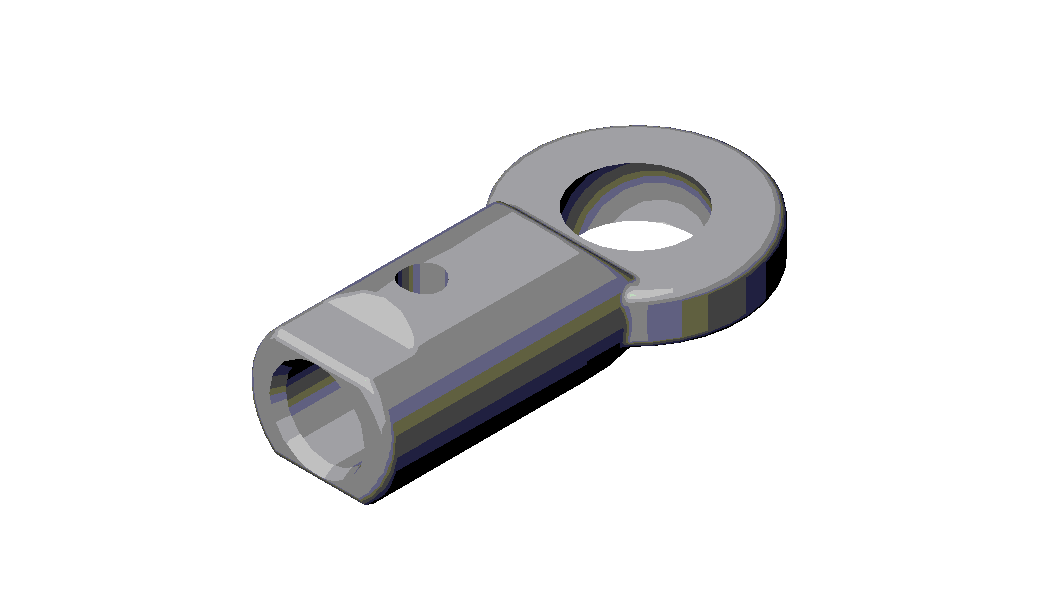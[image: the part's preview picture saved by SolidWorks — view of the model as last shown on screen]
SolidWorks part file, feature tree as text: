
SOLIDWORKS PART (.sldprt)
format: sldprt  version: not decoded by parser v0  size: 293,376 bytes
history: native  units: mm
features: sketch x7, plane x4, cut_extrude x2, fillet x2, material x1, revolve x1, extrude x1, hole x1 (+8 scaffold rows collapsed)
feature tree (27):
  scaffold x8  (default folders/planes/origin — collapsed)
  material  "Matériau <non spécifié>"
  plane  "Face"
  plane  "Dessus"
  plane  "Droite"
  plane  "Plan1"  Offset=67mm
  sketch  "Esquisse2"  dims[D1=30.0mm]
  sketch  "Esquisse1"  dims[D1=25.0mm D4=2.0mm D2=5.25mm D3=22.5mm]
  revolve  "Révolution1"  Angle=360deg
  extrude  "Extrusion2"  Depth=54mm
  sketch  "Esquisse3"  dims[c1.D1=~23.416655mm c2.D1=45.0deg c2.D2=11.0mm c2.D3=~8.19289mm c3.D3=45.0deg c3.D4=11.75mm]
  cut_extrude  "Enlèv. mat.-Extru.1"  [1 undecoded]
  fillet  "Congé5"  Radius=2mm
  fillet  "Congé7"  Radius=2mm
  sketch  "Esquisse5"
  hole  "Dégagement M1.61"  Diameter=18mm Depth=37mm
  sketch  "Esquisse11"
  sketch  "Esquisse10"  dims[hole-wizard template sketch: 39 standard entries collapsed; hole parameters kept: c13.Diamètre du perçage=18.0mm c13.Profondeur du perçage=37.0mm c13.Diamètre du fraisage entrant=20.0mm c13.D4=~33.297463mm c13.Angle du fraisage entrant=45.0deg c14.D5=~14.816244mm c14.Angle de pointe=118.0deg]
  sketch  "Esquisse12"  dims[D2=8.0mm D1=22.0mm]
  cut_extrude  "Enlèv. mat.-Extru.2"  [1 undecoded]
decode coverage: 10 of 14 modeling features carry decoded parameters
note: ~ marks probable driven/reference dimensions
note: 2 parameter values undecoded
note: suppression state not decoded; provenance and decode notes live in map.json
